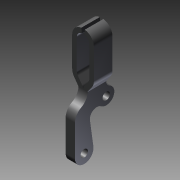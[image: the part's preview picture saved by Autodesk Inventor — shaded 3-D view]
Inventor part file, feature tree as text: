
AUTODESK INVENTOR PART (.ipt)
format: ipt  version: 2011 SP1 (Build 150282100, 282)  size: 156,672 bytes
history: native  units: mm
features: other x35, sketch x4, extrude x2, revolve x2
ambient origin geometry x8: Origin, YZ Plane, XZ Plane, XY Plane, X Axis, Y Axis, Z Axis, Center Point
bodies: Solid1 (feature_tree)
feature tree (43):
  extrude  "Extrusion1"  Depth=40.0mm TaperAngle=0.0deg
  extrude  "Extrusion2"  TaperAngle=360.0deg  [1 undecoded]
  revolve  "Revolution1"  [1 undecoded]
  revolve  "Revolution2"  [1 undecoded]
  other  "P1_XY"
  other  "P1_YZ"
  other  "P1_ZX"
  other  "P1_X"
  other  "P1_Y"
  other  "P1_Z"
  other  "P1_Center"
  other  "P2_XY"
  other  "P2_YZ"
  other  "P2_ZX"
  other  "P2_X"
  other  "P2_Y"
  other  "P2_Z"
  other  "P2_Center"
  other  "SA1_XY"
  other  "SA1_YZ"
  other  "SA1_ZX"
  other  "SA1_X"
  other  "SA1_Y"
  other  "SA1_Z"
  other  "SA1_Center"
  other  "SA2_XY"
  other  "SA2_YZ"
  other  "SA2_ZX"
  other  "SA2_X"
  other  "SA2_Y"
  other  "SA2_Z"
  other  "SA2_Center"
  other  "SA3_XY"
  other  "SA3_YZ"
  other  "SA3_ZX"
  other  "SA3_X"
  other  "SA3_Y"
  other  "SA3_Z"
  other  "SA3_Center"
  sketch  "Skizze_1"  dims[d0=40.0mm d1=0.0mm d2=40.0mm d3=0.0mm]
  sketch  "Skizze_2"
  sketch  "Skizze_3_ALT_Drilling_1"  dims[d4=360.0deg d5=360.0deg]
  sketch  "Skizze_4_ALT_Drilling_2"
note: 3 required parameter values undecoded (feature->parameter linkage not recoverable at this tier; creation-order binding heuristic only, values carry confidence <= 0.55)
